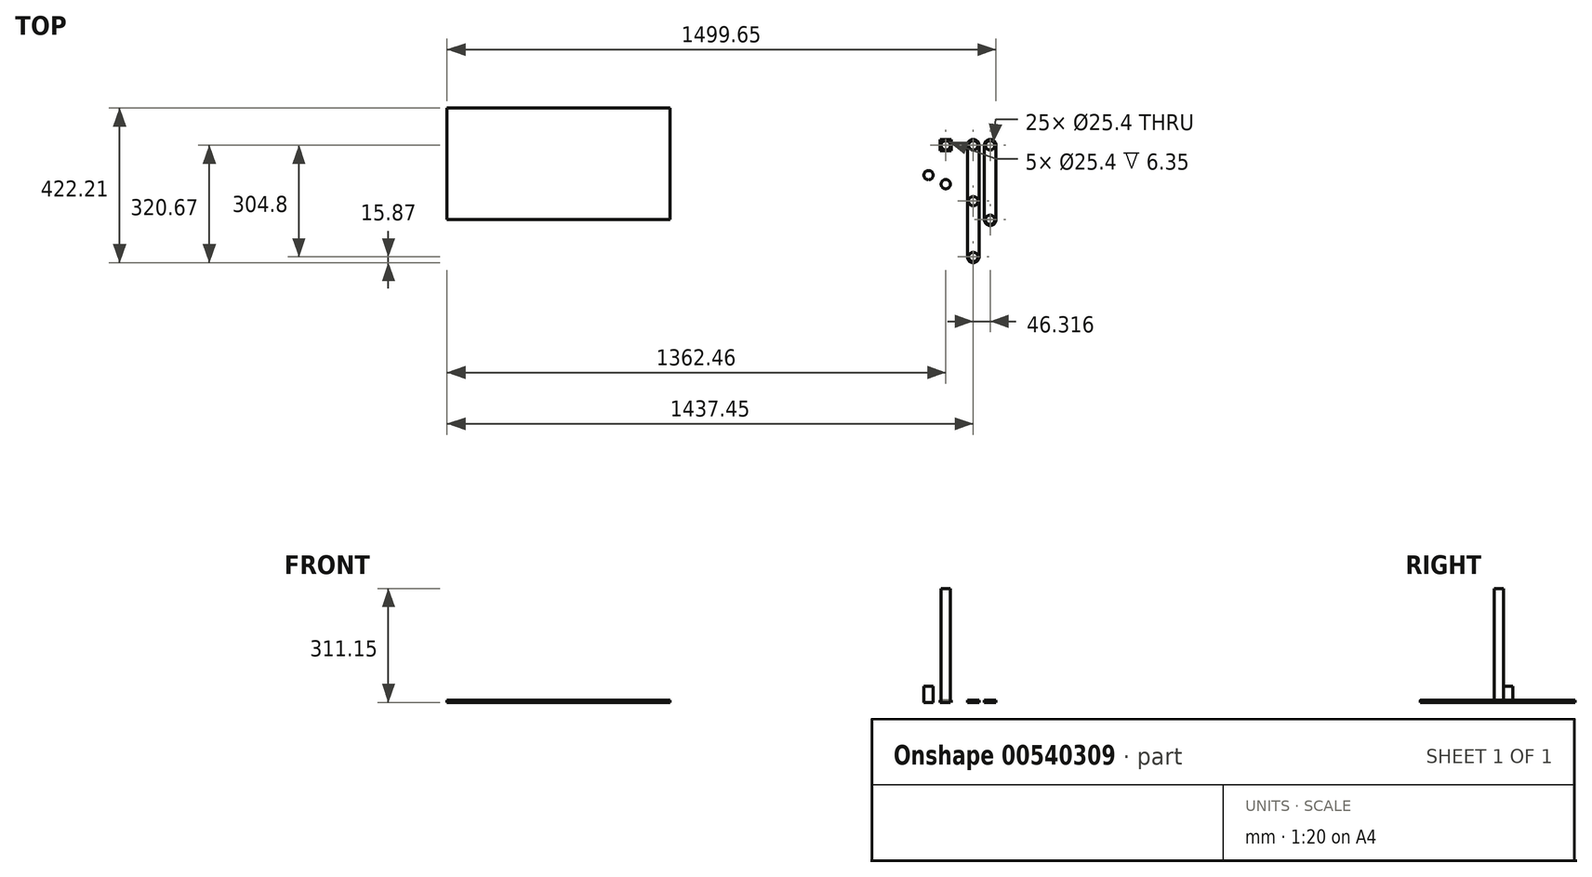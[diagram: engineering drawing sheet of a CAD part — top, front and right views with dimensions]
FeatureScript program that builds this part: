
annotation { "Feature Type Name" : "Feature", "Feature Type Description" : "" }
export const myFeature = defineFeature(function(context is Context, id is Id, definition is map)
    precondition{}
    {
        {
            var Q0;
            Q0=qCreatedBy(makeId("Top.planeOp"),FACE);
            var sketch = newSketch(context, id + "F0", { "sketchPlane" : qUnion([Q0])});
            skCircle(sketch, "E0", {"center": v(75.11, 50.86) * mm, "radius": 15.88 * mm});
            skCircle(sketch, "E1", {"center": v(75.11, 50.86) * mm, "radius": 12.7 * mm});
            skCircle(sketch, "E2", {"center": v(75.11, -253.94) * mm, "radius": 15.88 * mm});
            skCircle(sketch, "E3", {"center": v(75.11, -253.94) * mm, "radius": 12.7 * mm});
            skCircle(sketch, "E4", {"center": v(0, 50.86) * mm, "radius": 12.7 * mm});
            skCircle(sketch, "E5", {"center": v(121.31, 50.86) * mm, "radius": 15.88 * mm});
            skCircle(sketch, "E6", {"center": v(121.31, 50.86) * mm, "radius": 12.7 * mm});
            skCircle(sketch, "E7", {"center": v(121.31, -152.34) * mm, "radius": 15.88 * mm});
            skCircle(sketch, "E8", {"center": v(121.31, -152.34) * mm, "radius": 12.7 * mm});
            skCircle(sketch, "E9", {"center": v(-47.05, -30.61) * mm, "radius": 12.7 * mm});
            skLineSegment(sketch, "E10.bottom", {"start": v(15.14, 66.1) * mm, "end": v(-15.14, 66.1) * mm});
            skLineSegment(sketch, "E10.top", {"start": v(15.14, 35.63) * mm, "end": v(-15.14, 35.63) * mm});
            skLineSegment(sketch, "E10.left", {"start": v(15.14, 66.1) * mm, "end": v(15.14, 35.63) * mm});
            skLineSegment(sketch, "E10.right", {"start": v(-15.14, 66.1) * mm, "end": v(-15.14, 35.63) * mm});
            skLineSegment(sketch, "E11", {"start": v(59.24, 50.86) * mm, "end": v(59.24, -253.94) * mm});
            skLineSegment(sketch, "E12", {"start": v(90.99, 50.86) * mm, "end": v(90.99, -253.94) * mm});
            skLineSegment(sketch, "E13", {"start": v(105.44, 50.86) * mm, "end": v(105.44, -152.34) * mm});
            skLineSegment(sketch, "E14", {"start": v(137.19, 50.86) * mm, "end": v(137.19, -152.34) * mm});
            skPoint(sketch, "E15.centerSnap0", {"position": v(105.44, -50.74) * mm});
            skCircle(sketch, "E16", {"center": v(75, -101.54) * mm, "radius": 12.7 * mm});
            skPoint(sketch, "E16.centerSnap0", {"position": v(59.24, -101.54) * mm});
            skCircle(sketch, "E17", {"center": v(0, -55.28) * mm, "radius": 12.7 * mm});
            skSolve(sketch);
        }
        {
            var Q0;
            {var subQ0=sQuery(id+"F0.wireOp",EDGE,"E13");Q0=makeQuery(id+"F0.imprint","IMPRINT",FACE,{"disambiguationData":[TD([[makeQuery(id+"F0.imprint","IMPRINT",EDGE,{"derivedFrom":subQ0}),1.0]])]});}
            var Q1;
            {var subQ1=sQuery(id+"F0.wireOp",EDGE,"E11");Q1=makeQuery(id+"F0.imprint","IMPRINT",FACE,{"disambiguationData":[TD([[makeQuery(id+"F0.imprint","IMPRINT",EDGE,{"derivedFrom":subQ1}),1.0]])]});}
            var Q2;
            Q2=makeQuery(id+"F0.imprint","IMPRINT",FACE,{"disambiguationData":[TD([[makeQuery(id+"F0.imprint","IMPRINT",EDGE,{"derivedFrom":sQuery(id+"F0.wireOp",EDGE,"E1")}),-1.0]])]});
            var Q3;
            Q3=makeQuery(id+"F0.imprint","IMPRINT",FACE,{"disambiguationData":[TD([[makeQuery(id+"F0.imprint","IMPRINT",EDGE,{"derivedFrom":sQuery(id+"F0.wireOp",EDGE,"E6")}),-1.0]])]});
            var Q4;
            Q4=makeQuery(id+"F0.imprint","IMPRINT",FACE,{"disambiguationData":[TD([[makeQuery(id+"F0.imprint","IMPRINT",EDGE,{"derivedFrom":sQuery(id+"F0.wireOp",EDGE,"E8")}),-1.0]])]});
            var Q5;
            Q5=makeQuery(id+"F0.imprint","IMPRINT",FACE,{"disambiguationData":[TD([[makeQuery(id+"F0.imprint","IMPRINT",EDGE,{"derivedFrom":sQuery(id+"F0.wireOp",EDGE,"E3")}),-1.0]])]});
            var Q6;
            Q6=makeQuery(id+"F0.imprint","IMPRINT",FACE,{"disambiguationData":[TD([[makeQuery(id+"F0.imprint","IMPRINT",EDGE,{"derivedFrom":sQuery(id+"F0.wireOp",EDGE,"E4")}),-1.0]])]});
            var Q7;
            Q7=makeQuery(id+"F0.imprint","IMPRINT",FACE,{"disambiguationData":[TD([[makeQuery(id+"F0.imprint","IMPRINT",EDGE,{"derivedFrom":sQuery(id+"F0.wireOp",EDGE,"E17")}),1.0]])]});
            var Q8;
            Q8=makeQuery(id+"F0.imprint","IMPRINT",FACE,{"disambiguationData":[TD([[makeQuery(id+"F0.imprint","IMPRINT",EDGE,{"derivedFrom":sQuery(id+"F0.wireOp",EDGE,"E9")}),1.0]])]});
            extrude(context, id + "F1", {"entities" : qUnion([Q0, Q1, Q2, Q3, Q4, Q5, Q6, Q7, Q8]), "depth" : 6.35 * mm, "offsetDistance" : 25.4 * mm});
        }
        {
            var Q0;
            Q0=makeQuery(id+"F1.opExtrude","CAP_FACE",FACE,{"disambiguationData":[OSD([sQuery(id+"F0.wireOp",EDGE,"E9")])],"isStart":false});
            extrude(context, id + "F2", {"entities" : qUnion([Q0]), "operationType" : NewBodyOperationType.ADD, "depth" : 38.1 * mm, "offsetDistance" : 25.4 * mm});
        }
        {
            var Q0;
            Q0=makeQuery(id+"F1.opExtrude","CAP_FACE",FACE,{"disambiguationData":[OSD([sQuery(id+"F0.wireOp",EDGE,"E17")])],"isStart":false});
            extrude(context, id + "F3", {"entities" : qUnion([Q0]), "operationType" : NewBodyOperationType.ADD, "depth" : 304.8 * mm, "offsetDistance" : 25.4 * mm});
        }
        {
            var Q0;
            Q0=qCreatedBy(makeId("Top.planeOp"),FACE);
            var sketch = newSketch(context, id + "F4", { "sketchPlane" : qUnion([Q0])});
            skLineSegment(sketch, "E18.bottom", {"start": v(-1362.46, -152.4) * mm, "end": v(-752.86, -152.4) * mm});
            skLineSegment(sketch, "E18.top", {"start": v(-1362.46, 152.4) * mm, "end": v(-752.86, 152.4) * mm});
            skLineSegment(sketch, "E18.left", {"start": v(-1362.46, -152.4) * mm, "end": v(-1362.46, 152.4) * mm});
            skLineSegment(sketch, "E18.right", {"start": v(-752.86, -152.4) * mm, "end": v(-752.86, 152.4) * mm});
            skPoint(sketch, "E18.middle", {"position": v(-1057.66, 0) * mm});
            skLineSegment(sketch, "E19", {"start": v(-1057.66, 152.4) * mm, "end": v(-1057.66, -152.4) * mm, "construction": true});
            skSolve(sketch);
        }
        {
            var Q0;
            Q0=makeQuery(id+"F4.imprint","IMPRINT",FACE,{"disambiguationData":[TD([[makeQuery(id+"F4.imprint","IMPRINT",EDGE,{"derivedFrom":sQuery(id+"F4.wireOp",EDGE,"E18.bottom")}),1.0]])]});
            extrude(context, id + "F5", {"entities" : qUnion([Q0]), "depth" : 6.35 * mm, "offsetDistance" : 25.4 * mm});
        }
    });
